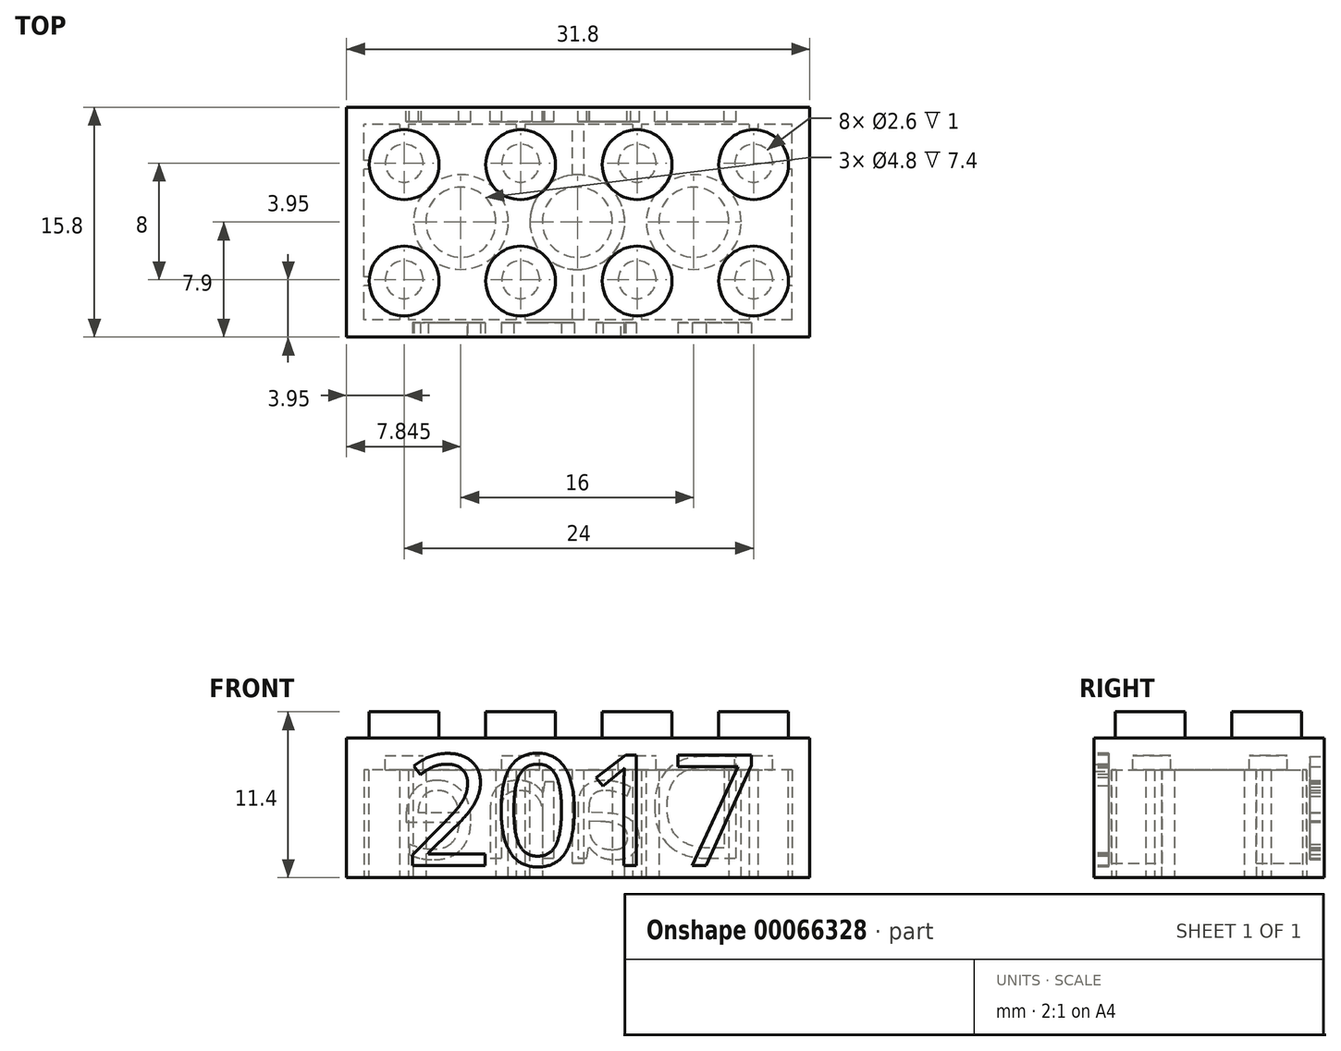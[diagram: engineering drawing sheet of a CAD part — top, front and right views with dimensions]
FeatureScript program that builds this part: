
annotation { "Feature Type Name" : "Feature", "Feature Type Description" : "" }
export const myFeature = defineFeature(function(context is Context, id is Id, definition is map)
    precondition{}
    {
        {
            var Q0;
            Q0=qCreatedBy(makeId("Top.planeOp"),FACE);
            var sketch = newSketch(context, id + "F0", { "sketchPlane" : qUnion([Q0])});
            skLineSegment(sketch, "E0.rect.bottom", {"start": v(15.9, -7.9) * mm, "end": v(-15.9, -7.9) * mm});
            skLineSegment(sketch, "E0.rect.top", {"start": v(15.9, 7.9) * mm, "end": v(-15.9, 7.9) * mm});
            skLineSegment(sketch, "E0.rect.left", {"start": v(15.9, -7.9) * mm, "end": v(15.9, 7.9) * mm});
            skLineSegment(sketch, "E0.rect.right", {"start": v(-15.9, -7.9) * mm, "end": v(-15.9, 7.9) * mm});
            skPoint(sketch, "E0.rect.middle", {"position": v(0, 0) * mm});
            skSolve(sketch);
        }
        {
            var Q0;
            Q0 = qSketchRegion(id + "F0", true);
            extrude(context, id + "F1", {"entities" : qUnion([Q0]), "depth" : 9.6 * mm});
        }
        {
            var Q0;
            Q0=qCreatedBy(makeId("Top.planeOp"),FACE);
            var sketch = newSketch(context, id + "F2", { "sketchPlane" : qUnion([Q0])});
            skLineSegment(sketch, "E1.rect.bottom", {"start": v(14.7, -6.7) * mm, "end": v(-14.7, -6.7) * mm});
            skLineSegment(sketch, "E1.rect.top", {"start": v(14.7, 6.7) * mm, "end": v(-14.7, 6.7) * mm});
            skLineSegment(sketch, "E1.rect.left", {"start": v(14.7, -6.7) * mm, "end": v(14.7, 6.7) * mm});
            skLineSegment(sketch, "E1.rect.right", {"start": v(-14.7, -6.7) * mm, "end": v(-14.7, 6.7) * mm});
            skPoint(sketch, "E1.rect.middle", {"position": v(0, 0) * mm});
            skSolve(sketch);
        }
        {
            var Q0;
            Q0=makeQuery(id+"F2.imprint","IMPRINT",FACE,{"disambiguationData":[TD([[makeQuery(id+"F2.imprint","IMPRINT",EDGE,{"derivedFrom":sQuery(id+"F2.wireOp",EDGE,"E1.rect.bottom")}),-1.0]])]});
            extrude(context, id + "F3", {"entities" : qUnion([Q0]), "operationType" : NewBodyOperationType.REMOVE, "depth" : 8.4 * mm});
        }
        {
            var Q0;
            Q0=makeQuery(id+"F1.opExtrude","CAP_FACE",FACE,{"disambiguationData":[OSD([sQuery(id+"F0.wireOp",EDGE,"E0.rect.bottom"),sQuery(id+"F0.wireOp",EDGE,"E0.rect.top"),sQuery(id+"F0.wireOp",EDGE,"E0.rect.left"),sQuery(id+"F0.wireOp",EDGE,"E0.rect.right")])],"isStart":false});
            var sketch = newSketch(context, id + "F4", { "sketchPlane" : qUnion([Q0])});
            skLineSegment(sketch, "E2", {"start": v(-18.39, 0) * mm, "end": v(19.33, 0) * mm, "construction": true});
            skPoint(sketch, "E2.startSnap0", {"position": v(-15.9, 0) * mm});
            skCircle(sketch, "E3", {"center": v(-11.95, 3.95) * mm, "radius": 2.4 * mm});
            skCircle(sketch, "E4.0.1.0", {"center": v(-11.95, -4.05) * mm, "radius": 2.4 * mm});
            skCircle(sketch, "E4.1.0.0", {"center": v(-3.95, 3.95) * mm, "radius": 2.4 * mm});
            skCircle(sketch, "E4.1.1.0", {"center": v(-3.95, -4.05) * mm, "radius": 2.4 * mm});
            skCircle(sketch, "E4.2.0.0", {"center": v(4.05, 3.95) * mm, "radius": 2.4 * mm});
            skCircle(sketch, "E4.2.1.0", {"center": v(4.05, -4.05) * mm, "radius": 2.4 * mm});
            skCircle(sketch, "E4.3.0.0", {"center": v(12.05, 3.95) * mm, "radius": 2.4 * mm});
            skCircle(sketch, "E4.3.1.0", {"center": v(12.05, -4.05) * mm, "radius": 2.4 * mm});
            skLineSegment(sketch, "E4.direction1", {"start": v(-11.95, 3.95) * mm, "end": v(-3.95, 3.95) * mm, "construction": true});
            skLineSegment(sketch, "E4.direction2", {"start": v(-11.95, 3.95) * mm, "end": v(-11.95, -4.05) * mm, "construction": true});
            skLineSegment(sketch, "E5", {"start": v(-11.95, -4.05) * mm, "end": v(-11.95, -9.52) * mm, "construction": true});
            skLineSegment(sketch, "E6", {"start": v(-11.95, -9.52) * mm, "end": v(-11.95, 12.13) * mm, "construction": true});
            skLineSegment(sketch, "E7", {"start": v(-11.95, 12.13) * mm, "end": v(-11.95, 3.95) * mm, "construction": true});
            skLineSegment(sketch, "E8", {"start": v(-11.95, 3.95) * mm, "end": v(-19.65, 3.95) * mm, "construction": true});
            skLineSegment(sketch, "E9", {"start": v(-19.65, 3.95) * mm, "end": v(20.22, 3.95) * mm, "construction": true});
            skLineSegment(sketch, "E10", {"start": v(20.22, 3.95) * mm, "end": v(12.05, 3.95) * mm, "construction": true});
            skLineSegment(sketch, "E11", {"start": v(12.05, 3.95) * mm, "end": v(12.05, 11.38) * mm, "construction": true});
            skLineSegment(sketch, "E12", {"start": v(12.05, 11.38) * mm, "end": v(12.05, -12.57) * mm, "construction": true});
            skLineSegment(sketch, "E13", {"start": v(12.05, -12.57) * mm, "end": v(12.05, -4.05) * mm, "construction": true});
            skLineSegment(sketch, "E14", {"start": v(4.05, -4.05) * mm, "end": v(4.05, -12.47) * mm, "construction": true});
            skLineSegment(sketch, "E15", {"start": v(4.05, -12.47) * mm, "end": v(4.05, 12.59) * mm, "construction": true});
            skLineSegment(sketch, "E16", {"start": v(4.05, 12.59) * mm, "end": v(4.05, 3.95) * mm, "construction": true});
            skLineSegment(sketch, "E17", {"start": v(-3.95, 3.95) * mm, "end": v(-3.95, 12.2) * mm, "construction": true});
            skLineSegment(sketch, "E18", {"start": v(-3.95, 12.2) * mm, "end": v(-3.95, -12.51) * mm, "construction": true});
            skLineSegment(sketch, "E19", {"start": v(-3.95, -12.51) * mm, "end": v(-3.95, -4.05) * mm, "construction": true});
            skLineSegment(sketch, "E20", {"start": v(-11.95, -4.05) * mm, "end": v(-20.42, -4.05) * mm, "construction": true});
            skLineSegment(sketch, "E21", {"start": v(-20.42, -4.05) * mm, "end": v(-11.95, -4.05) * mm, "construction": true});
            skLineSegment(sketch, "E22", {"start": v(-11.95, -4.05) * mm, "end": v(20.33, -4.05) * mm, "construction": true});
            skSolve(sketch);
        }
        {
            var Q0;
            Q0=makeQuery(id+"F4.imprint","IMPRINT",FACE,{"disambiguationData":[TD([[makeQuery(id+"F4.imprint","IMPRINT",EDGE,{"derivedFrom":sQuery(id+"F4.wireOp",EDGE,"E3")}),1.0]])]});
            var Q1;
            Q1=makeQuery(id+"F4.imprint","IMPRINT",FACE,{"disambiguationData":[TD([[makeQuery(id+"F4.imprint","IMPRINT",EDGE,{"derivedFrom":sQuery(id+"F4.wireOp",EDGE,"E4.0.1.0")}),1.0]])]});
            var Q2;
            Q2=makeQuery(id+"F4.imprint","IMPRINT",FACE,{"disambiguationData":[TD([[makeQuery(id+"F4.imprint","IMPRINT",EDGE,{"derivedFrom":sQuery(id+"F4.wireOp",EDGE,"E4.1.1.0")}),1.0]])]});
            var Q3;
            Q3=makeQuery(id+"F4.imprint","IMPRINT",FACE,{"disambiguationData":[TD([[makeQuery(id+"F4.imprint","IMPRINT",EDGE,{"derivedFrom":sQuery(id+"F4.wireOp",EDGE,"E4.2.0.0")}),1.0]])]});
            var Q4;
            Q4=makeQuery(id+"F4.imprint","IMPRINT",FACE,{"disambiguationData":[TD([[makeQuery(id+"F4.imprint","IMPRINT",EDGE,{"derivedFrom":sQuery(id+"F4.wireOp",EDGE,"E4.1.0.0")}),1.0]])]});
            var Q5;
            Q5=makeQuery(id+"F4.imprint","IMPRINT",FACE,{"disambiguationData":[TD([[makeQuery(id+"F4.imprint","IMPRINT",EDGE,{"derivedFrom":sQuery(id+"F4.wireOp",EDGE,"E4.2.1.0")}),1.0]])]});
            var Q6;
            Q6=makeQuery(id+"F4.imprint","IMPRINT",FACE,{"disambiguationData":[TD([[makeQuery(id+"F4.imprint","IMPRINT",EDGE,{"derivedFrom":sQuery(id+"F4.wireOp",EDGE,"E4.3.1.0")}),1.0]])]});
            var Q7;
            Q7=makeQuery(id+"F4.imprint","IMPRINT",FACE,{"disambiguationData":[TD([[makeQuery(id+"F4.imprint","IMPRINT",EDGE,{"derivedFrom":sQuery(id+"F4.wireOp",EDGE,"E4.3.0.0")}),1.0]])]});
            extrude(context, id + "F5", {"entities" : qUnion([Q0, Q1, Q2, Q3, Q4, Q5, Q6, Q7]), "operationType" : NewBodyOperationType.ADD, "depth" : 1.8 * mm});
        }
        {
            var Q0;
            Q0=makeQuery(id+"F3.boolean.opBoolean","COPY",FACE,{"derivedFrom":makeQuery(id+"F3.opExtrude","CAP_FACE",FACE,{"disambiguationData":[OSD([sQuery(id+"F2.wireOp",EDGE,"E1.rect.bottom"),sQuery(id+"F2.wireOp",EDGE,"E1.rect.top"),sQuery(id+"F2.wireOp",EDGE,"E1.rect.left"),sQuery(id+"F2.wireOp",EDGE,"E1.rect.right")])],"isStart":false})});
            var sketch = newSketch(context, id + "F6", { "sketchPlane" : qUnion([Q0])});
            skCircle(sketch, "E23", {"center": v(-11.95, 3.95) * mm, "radius": 1.3 * mm});
            skCircle(sketch, "E24.0.1.0", {"center": v(-11.95, -4.05) * mm, "radius": 1.3 * mm});
            skCircle(sketch, "E24.1.0.0", {"center": v(-3.95, 3.95) * mm, "radius": 1.3 * mm});
            skCircle(sketch, "E24.1.1.0", {"center": v(-3.95, -4.05) * mm, "radius": 1.3 * mm});
            skCircle(sketch, "E24.2.0.0", {"center": v(4.05, 3.95) * mm, "radius": 1.3 * mm});
            skCircle(sketch, "E24.2.1.0", {"center": v(4.05, -4.05) * mm, "radius": 1.3 * mm});
            skCircle(sketch, "E24.3.0.0", {"center": v(12.05, 3.95) * mm, "radius": 1.3 * mm});
            skCircle(sketch, "E24.3.1.0", {"center": v(12.05, -4.05) * mm, "radius": 1.3 * mm});
            skLineSegment(sketch, "E24.direction1", {"start": v(-11.95, 3.95) * mm, "end": v(-3.95, 3.95) * mm, "construction": true});
            skLineSegment(sketch, "E24.direction2", {"start": v(-11.95, 3.95) * mm, "end": v(-11.95, -4.05) * mm, "construction": true});
            skLineSegment(sketch, "E25", {"start": v(12.05, -4.05) * mm, "end": v(4.05, 3.95) * mm, "construction": true});
            skLineSegment(sketch, "E26", {"start": v(-3.95, -4.05) * mm, "end": v(4.05, 5.25) * mm, "construction": true});
            skLineSegment(sketch, "E27", {"start": v(4.05, 5.25) * mm, "end": v(-3.95, -4.05) * mm, "construction": true});
            skLineSegment(sketch, "E28", {"start": v(-3.95, -4.05) * mm, "end": v(-11.95, 3.95) * mm, "construction": true});
            skLineSegment(sketch, "E29", {"start": v(12.05, 3.95) * mm, "end": v(4.05, -4.05) * mm, "construction": true});
            skLineSegment(sketch, "E30", {"start": v(4.05, -4.05) * mm, "end": v(-3.95, 3.95) * mm, "construction": true});
            skLineSegment(sketch, "E31", {"start": v(-3.95, 3.95) * mm, "end": v(-11.95, -4.05) * mm, "construction": true});
            skSolve(sketch);
        }
        {
            var Q0;
            Q0=makeQuery(id+"F6.imprint","IMPRINT",FACE,{"disambiguationData":[TD([[makeQuery(id+"F6.imprint","IMPRINT",EDGE,{"derivedFrom":sQuery(id+"F6.wireOp",EDGE,"E23")}),-1.0]])]});
            extrude(context, id + "F7", {"entities" : qUnion([Q0]), "operationType" : NewBodyOperationType.ADD, "depth" : 1 * mm});
        }
        {
            var Q0;
            Q0=makeQuery(id+"F7.opExtrude","CAP_FACE",FACE,{"disambiguationData":[OSD([sQuery(id+"F2.wireOp",EDGE,"E1.rect.bottom"),sQuery(id+"F2.wireOp",EDGE,"E1.rect.top"),sQuery(id+"F2.wireOp",EDGE,"E1.rect.left"),sQuery(id+"F2.wireOp",EDGE,"E1.rect.right"),sQuery(id+"F6.wireOp",EDGE,"E23"),sQuery(id+"F6.wireOp",EDGE,"E24.0.1.0"),sQuery(id+"F6.wireOp",EDGE,"E24.1.0.0"),sQuery(id+"F6.wireOp",EDGE,"E24.1.1.0"),sQuery(id+"F6.wireOp",EDGE,"E24.2.0.0"),sQuery(id+"F6.wireOp",EDGE,"E24.2.1.0"),sQuery(id+"F6.wireOp",EDGE,"E24.3.0.0"),sQuery(id+"F6.wireOp",EDGE,"E24.3.1.0")])],"isStart":false});
            var sketch = newSketch(context, id + "F8", { "sketchPlane" : qUnion([Q0])});
            skCircle(sketch, "E32", {"center": v(7.95, 0) * mm, "radius": 3.25 * mm});
            skCircle(sketch, "E33.1.0.0", {"center": v(-0.05, 0) * mm, "radius": 3.25 * mm});
            skCircle(sketch, "E33.2.0.0", {"center": v(-8.05, 0) * mm, "radius": 3.25 * mm});
            skLineSegment(sketch, "E33.direction1", {"start": v(7.95, 0) * mm, "end": v(-0.05, 0) * mm, "construction": true});
            skSolve(sketch);
        }
        {
            var Q0;
            Q0 = qSketchRegion(id + "F8", true);
            extrude(context, id + "F9", {"entities" : qUnion([Q0]), "operationType" : NewBodyOperationType.ADD, "depth" : 7.4 * mm});
        }
        {
            var Q0;
            Q0=makeQuery(id+"F9.opExtrude","CAP_FACE",FACE,{"disambiguationData":[OSD([sQuery(id+"F8.wireOp",EDGE,"E33.2.0.0")])],"isStart":false});
            var sketch = newSketch(context, id + "F10", { "sketchPlane" : qUnion([Q0])});
            skCircle(sketch, "E34", {"center": v(-8.05, 0) * mm, "radius": 2.4 * mm});
            skCircle(sketch, "E35.1.0.0", {"center": v(-0.05, 0) * mm, "radius": 2.4 * mm});
            skCircle(sketch, "E35.2.0.0", {"center": v(7.95, 0) * mm, "radius": 2.4 * mm});
            skLineSegment(sketch, "E35.direction1", {"start": v(-8.05, 0) * mm, "end": v(-0.05, 0) * mm, "construction": true});
            skSolve(sketch);
        }
        {
            var Q0;
            Q0=makeQuery(id+"F10.imprint","IMPRINT",FACE,{"disambiguationData":[TD([[makeQuery(id+"F10.imprint","IMPRINT",EDGE,{"derivedFrom":sQuery(id+"F10.wireOp",EDGE,"E34")}),1.0]])]});
            var Q1;
            Q1=makeQuery(id+"F10.imprint","IMPRINT",FACE,{"disambiguationData":[TD([[makeQuery(id+"F10.imprint","IMPRINT",EDGE,{"derivedFrom":sQuery(id+"F10.wireOp",EDGE,"E35.1.0.0")}),1.0]])]});
            var Q2;
            Q2=makeQuery(id+"F10.imprint","IMPRINT",FACE,{"disambiguationData":[TD([[makeQuery(id+"F10.imprint","IMPRINT",EDGE,{"derivedFrom":sQuery(id+"F10.wireOp",EDGE,"E35.2.0.0")}),1.0]])]});
            extrude(context, id + "F11", {"entities" : qUnion([Q0, Q1, Q2]), "operationType" : NewBodyOperationType.REMOVE, "oppositeDirection" : true, "depth" : 7.4 * mm});
        }
        {
            var Q0;
            Q0=makeQuery(id+"F7.opExtrude","CAP_FACE",FACE,{"disambiguationData":[OSD([sQuery(id+"F2.wireOp",EDGE,"E1.rect.bottom"),sQuery(id+"F2.wireOp",EDGE,"E1.rect.top"),sQuery(id+"F2.wireOp",EDGE,"E1.rect.left"),sQuery(id+"F2.wireOp",EDGE,"E1.rect.right"),sQuery(id+"F6.wireOp",EDGE,"E23"),sQuery(id+"F6.wireOp",EDGE,"E24.0.1.0"),sQuery(id+"F6.wireOp",EDGE,"E24.1.0.0"),sQuery(id+"F6.wireOp",EDGE,"E24.1.1.0"),sQuery(id+"F6.wireOp",EDGE,"E24.2.0.0"),sQuery(id+"F6.wireOp",EDGE,"E24.2.1.0"),sQuery(id+"F6.wireOp",EDGE,"E24.3.0.0"),sQuery(id+"F6.wireOp",EDGE,"E24.3.1.0")])],"isStart":false});
            var sketch = newSketch(context, id + "F12", { "sketchPlane" : qUnion([Q0])});
            skLineSegment(sketch, "E36.rect.bottom", {"start": v(0.4, 6.7) * mm, "end": v(-0.4, 6.7) * mm});
            skLineSegment(sketch, "E36.rect.top", {"start": v(0.4, -6.7) * mm, "end": v(-0.4, -6.7) * mm});
            skLineSegment(sketch, "E36.rect.left", {"start": v(0.4, 6.7) * mm, "end": v(0.4, -6.7) * mm});
            skLineSegment(sketch, "E36.rect.right", {"start": v(-0.4, 6.7) * mm, "end": v(-0.4, -6.7) * mm});
            skPoint(sketch, "E36.rect.middle", {"position": v(0, 0) * mm});
            skSolve(sketch);
        }
        {
            var Q0;
            Q0 = qSketchRegion(id + "F12", true);
            extrude(context, id + "F13", {"entities" : qUnion([Q0]), "operationType" : NewBodyOperationType.ADD, "depth" : 6.4 * mm});
        }
        {
            var Q0;
            {var subQ0=sQuery(id+"F12.wireOp",EDGE,"E36.rect.left");var subQ1=sQuery(id+"F12.wireOp",EDGE,"E36.rect.right");Q0=makeQuery(id+"F13.boolean.opBoolean","SPLIT",FACE,{"disambiguationData":[TD([makeQuery(id+"F11.boolean.opBoolean","COPY",FACE,{"derivedFrom":makeQuery(id+"F11.opExtrude","SWEPT_FACE",FACE,{"disambiguationData":[OSD([sQuery(id+"F10.wireOp",EDGE,"E35.1.0.0")])]})})])],"derivedFrom":makeQuery(id+"F13.opExtrude","CAP_FACE",FACE,{"disambiguationData":[OSD([sQuery(id+"F12.wireOp",EDGE,"E36.rect.bottom"),sQuery(id+"F12.wireOp",EDGE,"E36.rect.top"),subQ0,subQ1])],"isStart":false})});}
            var sketch = newSketch(context, id + "F14", { "sketchPlane" : qUnion([Q0])});
            skSolve(sketch);
        }
        {
            var Q0;
            {var subQ0=makeQuery(id+"F11.boolean.opBoolean","COPY",FACE,{"derivedFrom":makeQuery(id+"F11.opExtrude","SWEPT_FACE",FACE,{"disambiguationData":[OSD([sQuery(id+"F10.wireOp",EDGE,"E35.1.0.0")])]})});var subQ1=sQuery(id+"F12.wireOp",EDGE,"E36.rect.right");var subQ2=sQuery(id+"F12.wireOp",EDGE,"E36.rect.left");var subQ3=makeQuery(id+"F13.opExtrude","CAP_FACE",FACE,{"disambiguationData":[OSD([sQuery(id+"F12.wireOp",EDGE,"E36.rect.bottom"),sQuery(id+"F12.wireOp",EDGE,"E36.rect.top"),subQ2,subQ1])],"isStart":false});Q0=makeQuery(id+"F14.imprint","IMPRINT",FACE,{"disambiguationData":[TD([[makeQuery(id+"F14.imprint","IMPRINT",EDGE,{"derivedFrom":makeQuery(id+"F13.boolean.opBoolean","INTERSECT",EDGE,{"disambiguationData":[OD(0.0)],"derivedFrom":[subQ0,subQ3]})}),-1.0]])]});}
            extrude(context, id + "F15", {"entities" : qUnion([Q0]), "operationType" : NewBodyOperationType.REMOVE, "oppositeDirection" : true, "depth" : 6.4 * mm});
        }
        {
            var Q0;
            Q0=makeQuery(id+"F1.opExtrude","CAP_FACE",FACE,{"disambiguationData":[OSD([sQuery(id+"F0.wireOp",EDGE,"E0.rect.bottom"),sQuery(id+"F0.wireOp",EDGE,"E0.rect.top"),sQuery(id+"F0.wireOp",EDGE,"E0.rect.left"),sQuery(id+"F0.wireOp",EDGE,"E0.rect.right")])],"isStart":true});
            var sketch = newSketch(context, id + "F16", { "sketchPlane" : qUnion([Q0])});
            skLineSegment(sketch, "E37.bottom", {"start": v(-12.25, 6.7) * mm, "end": v(-11.65, 6.7) * mm});
            skLineSegment(sketch, "E37.top", {"start": v(-12.25, 6.4) * mm, "end": v(-11.65, 6.4) * mm});
            skLineSegment(sketch, "E37.left", {"start": v(-12.25, 6.7) * mm, "end": v(-12.25, 6.4) * mm});
            skLineSegment(sketch, "E37.right", {"start": v(-11.65, 6.7) * mm, "end": v(-11.65, 6.4) * mm});
            skLineSegment(sketch, "E38.0.1.0", {"start": v(-12.25, -6.4) * mm, "end": v(-11.65, -6.4) * mm});
            skLineSegment(sketch, "E38.0.1.1", {"start": v(-11.65, -6.4) * mm, "end": v(-11.65, -6.7) * mm});
            skLineSegment(sketch, "E38.0.1.2", {"start": v(-12.25, -6.7) * mm, "end": v(-11.65, -6.7) * mm});
            skLineSegment(sketch, "E38.0.1.3", {"start": v(-12.25, -6.4) * mm, "end": v(-12.25, -6.7) * mm});
            skLineSegment(sketch, "E38.1.0.0", {"start": v(-4.25, 6.7) * mm, "end": v(-3.65, 6.7) * mm});
            skLineSegment(sketch, "E38.1.0.1", {"start": v(-3.65, 6.7) * mm, "end": v(-3.65, 6.4) * mm});
            skLineSegment(sketch, "E38.1.0.2", {"start": v(-4.25, 6.4) * mm, "end": v(-3.65, 6.4) * mm});
            skLineSegment(sketch, "E38.1.0.3", {"start": v(-4.25, 6.7) * mm, "end": v(-4.25, 6.4) * mm});
            skLineSegment(sketch, "E38.1.1.0", {"start": v(-4.25, -6.4) * mm, "end": v(-3.65, -6.4) * mm});
            skLineSegment(sketch, "E38.1.1.1", {"start": v(-3.65, -6.4) * mm, "end": v(-3.65, -6.7) * mm});
            skLineSegment(sketch, "E38.1.1.2", {"start": v(-4.25, -6.7) * mm, "end": v(-3.65, -6.7) * mm});
            skLineSegment(sketch, "E38.1.1.3", {"start": v(-4.25, -6.4) * mm, "end": v(-4.25, -6.7) * mm});
            skLineSegment(sketch, "E38.2.0.0", {"start": v(3.75, 6.7) * mm, "end": v(4.35, 6.7) * mm});
            skLineSegment(sketch, "E38.2.0.1", {"start": v(4.35, 6.7) * mm, "end": v(4.35, 6.4) * mm});
            skLineSegment(sketch, "E38.2.0.2", {"start": v(3.75, 6.4) * mm, "end": v(4.35, 6.4) * mm});
            skLineSegment(sketch, "E38.2.0.3", {"start": v(3.75, 6.7) * mm, "end": v(3.75, 6.4) * mm});
            skLineSegment(sketch, "E38.2.1.0", {"start": v(3.75, -6.4) * mm, "end": v(4.35, -6.4) * mm});
            skLineSegment(sketch, "E38.2.1.1", {"start": v(4.35, -6.4) * mm, "end": v(4.35, -6.7) * mm});
            skLineSegment(sketch, "E38.2.1.2", {"start": v(3.75, -6.7) * mm, "end": v(4.35, -6.7) * mm});
            skLineSegment(sketch, "E38.2.1.3", {"start": v(3.75, -6.4) * mm, "end": v(3.75, -6.7) * mm});
            skLineSegment(sketch, "E38.3.0.0", {"start": v(11.75, 6.7) * mm, "end": v(12.35, 6.7) * mm});
            skLineSegment(sketch, "E38.3.0.1", {"start": v(12.35, 6.7) * mm, "end": v(12.35, 6.4) * mm});
            skLineSegment(sketch, "E38.3.0.2", {"start": v(11.75, 6.4) * mm, "end": v(12.35, 6.4) * mm});
            skLineSegment(sketch, "E38.3.0.3", {"start": v(11.75, 6.7) * mm, "end": v(11.75, 6.4) * mm});
            skLineSegment(sketch, "E38.3.1.0", {"start": v(11.75, -6.4) * mm, "end": v(12.35, -6.4) * mm});
            skLineSegment(sketch, "E38.3.1.1", {"start": v(12.35, -6.4) * mm, "end": v(12.35, -6.7) * mm});
            skLineSegment(sketch, "E38.3.1.2", {"start": v(11.75, -6.7) * mm, "end": v(12.35, -6.7) * mm});
            skLineSegment(sketch, "E38.3.1.3", {"start": v(11.75, -6.4) * mm, "end": v(11.75, -6.7) * mm});
            skLineSegment(sketch, "E38.direction1", {"start": v(-12.25, 6.7) * mm, "end": v(-4.25, 6.7) * mm, "construction": true});
            skLineSegment(sketch, "E38.direction2", {"start": v(-12.25, 6.7) * mm, "end": v(-12.25, -6.4) * mm, "construction": true});
            skSolve(sketch);
        }
        {
            var Q0;
            Q0 = qSketchRegion(id + "F16", true);
            extrude(context, id + "F17", {"entities" : qUnion([Q0]), "operationType" : NewBodyOperationType.ADD, "endBound" : BoundingType.UP_TO_NEXT, "oppositeDirection" : true, "depth" : 7.4 * mm});
        }
        {
            var Q0;
            {var subQ8=sQuery(id+"F16.wireOp",EDGE,"E37.bottom");Q0=makeQuery(id+"F16.imprint","IMPRINT",FACE,{"disambiguationData":[TD([[makeQuery(id+"F16.imprint","IMPRINT",EDGE,{"derivedFrom":subQ8}),-1.0]])]});}
            var sketch = newSketch(context, id + "F18", { "sketchPlane" : qUnion([Q0])});
            skLineSegment(sketch, "E39.bottom", {"start": v(-14.7, 4.35) * mm, "end": v(-14.4, 4.35) * mm});
            skLineSegment(sketch, "E39.top", {"start": v(-14.7, 3.75) * mm, "end": v(-14.4, 3.75) * mm});
            skLineSegment(sketch, "E39.left", {"start": v(-14.7, 4.35) * mm, "end": v(-14.7, 3.75) * mm});
            skLineSegment(sketch, "E39.right", {"start": v(-14.4, 4.35) * mm, "end": v(-14.4, 3.75) * mm});
            skLineSegment(sketch, "E40.0.1.0", {"start": v(-14.4, -3.65) * mm, "end": v(-14.4, -4.25) * mm});
            skLineSegment(sketch, "E40.0.1.1", {"start": v(-14.7, -3.65) * mm, "end": v(-14.4, -3.65) * mm});
            skLineSegment(sketch, "E40.0.1.2", {"start": v(-14.7, -3.65) * mm, "end": v(-14.7, -4.25) * mm});
            skLineSegment(sketch, "E40.0.1.3", {"start": v(-14.7, -4.25) * mm, "end": v(-14.4, -4.25) * mm});
            skLineSegment(sketch, "E40.1.0.0", {"start": v(14.7, 4.35) * mm, "end": v(14.7, 3.75) * mm});
            skLineSegment(sketch, "E40.1.0.1", {"start": v(14.4, 4.35) * mm, "end": v(14.7, 4.35) * mm});
            skLineSegment(sketch, "E40.1.0.2", {"start": v(14.4, 4.35) * mm, "end": v(14.4, 3.75) * mm});
            skLineSegment(sketch, "E40.1.0.3", {"start": v(14.4, 3.75) * mm, "end": v(14.7, 3.75) * mm});
            skLineSegment(sketch, "E40.1.1.0", {"start": v(14.7, -3.65) * mm, "end": v(14.7, -4.25) * mm});
            skLineSegment(sketch, "E40.1.1.1", {"start": v(14.4, -3.65) * mm, "end": v(14.7, -3.65) * mm});
            skLineSegment(sketch, "E40.1.1.2", {"start": v(14.4, -3.65) * mm, "end": v(14.4, -4.25) * mm});
            skLineSegment(sketch, "E40.1.1.3", {"start": v(14.4, -4.25) * mm, "end": v(14.7, -4.25) * mm});
            skLineSegment(sketch, "E40.direction1", {"start": v(-14.4, 3.75) * mm, "end": v(14.7, 3.75) * mm, "construction": true});
            skLineSegment(sketch, "E40.direction2", {"start": v(-14.4, 3.75) * mm, "end": v(-14.4, -4.25) * mm, "construction": true});
            skSolve(sketch);
        }
        {
            var Q0;
            Q0 = qSketchRegion(id + "F18", true);
            extrude(context, id + "F19", {"entities" : qUnion([Q0]), "operationType" : NewBodyOperationType.ADD, "endBound" : BoundingType.UP_TO_NEXT, "oppositeDirection" : true, "depth" : 25 * mm});
        }
        {
            var Q0;
            Q0=makeQuery(id+"F1.opExtrude","SWEPT_FACE",FACE,{"disambiguationData":[OSD([sQuery(id+"F0.wireOp",EDGE,"E0.rect.top")])]});
            var sketch = newSketch(context, id + "F20", { "sketchPlane" : qUnion([Q0])});
            skText(sketch, "E41", { "text": "Dane\n", "fontName": "OpenSans-Regular.ttf"});
            const initialGuessF20  = {"E41": [-0.0118, 0.00134, 1, 0, 0.00706]};
            skSetInitialGuess(sketch, initialGuessF20);
            skSolve(sketch);
        }
        {
            var Q0;
            Q0 = qSketchRegion(id + "F20", true);
            extrude(context, id + "F21", {"entities" : qUnion([Q0]), "operationType" : NewBodyOperationType.REMOVE, "oppositeDirection" : true, "depth" : 1 * mm});
        }
        {
            var Q0;
            Q0=makeQuery(id+"F1.opExtrude","SWEPT_FACE",FACE,{"disambiguationData":[OSD([sQuery(id+"F0.wireOp",EDGE,"E0.rect.bottom")])]});
            var sketch = newSketch(context, id + "F22", { "sketchPlane" : qUnion([Q0])});
            skText(sketch, "E42", { "text": "2017", "fontName": "OpenSans-Regular.ttf"});
            const initialGuessF22  = {"E42": [-0.0119, 0.00084, 1, 0, 0.00766]};
            skSetInitialGuess(sketch, initialGuessF22);
            skSolve(sketch);
        }
        {
            var Q0;
            Q0 = qSketchRegion(id + "F22", true);
            extrude(context, id + "F23", {"entities" : qUnion([Q0]), "operationType" : NewBodyOperationType.REMOVE, "oppositeDirection" : true, "depth" : 1 * mm});
        }
    });
